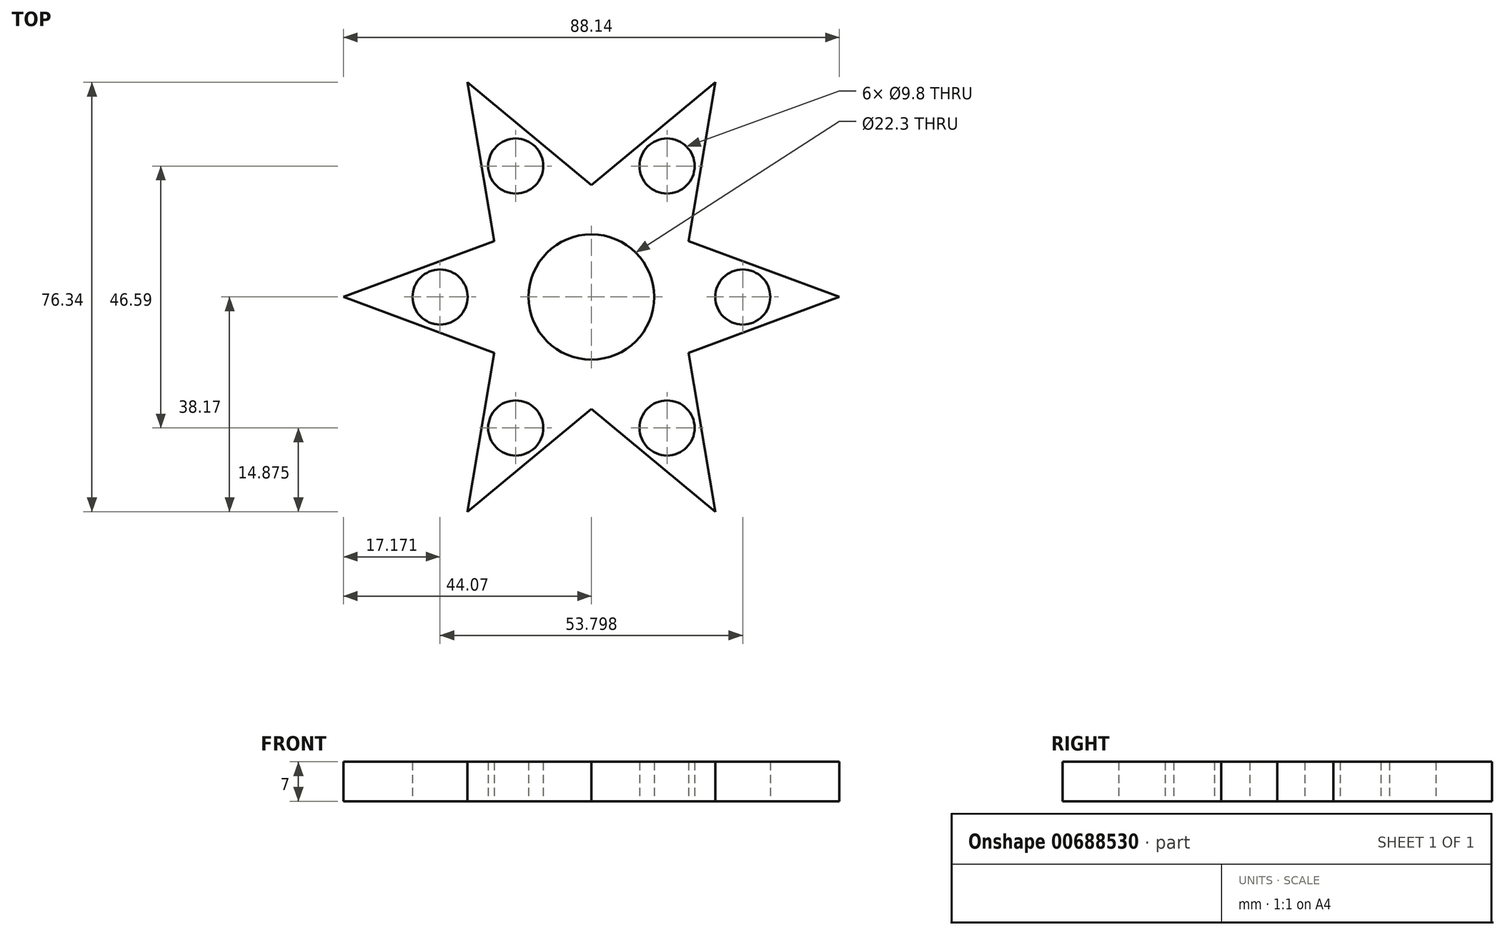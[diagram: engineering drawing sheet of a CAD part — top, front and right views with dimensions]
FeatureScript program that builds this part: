
annotation { "Feature Type Name" : "Feature", "Feature Type Description" : "" }
export const myFeature = defineFeature(function(context is Context, id is Id, definition is map)
    precondition{}
    {
        {
            var Q0;
            Q0=qCreatedBy(makeId("Top.planeOp"),FACE);
            var sketch = newSketch(context, id + "F0", { "sketchPlane" : qUnion([Q0])});
            skCircle(sketch, "E0", {"center": v(0, 0) * mm, "radius": 11.15 * mm});
            skCircle(sketch, "E1", {"center": v(0, 0) * mm, "radius": 15.38 * mm});
            skLineSegment(sketch, "E2", {"start": v(6.42, 13.98) * mm, "end": v(44.07, 0) * mm});
            skLineSegment(sketch, "E3.MirrorCS", {"start": v(6.42, -13.98) * mm, "end": v(44.07, 0) * mm});
            skCircle(sketch, "E4", {"center": v(26.9, 0) * mm, "radius": 4.9 * mm});
            skCircle(sketch, "E5.1.0", {"center": v(13.45, 23.3) * mm, "radius": 4.9 * mm});
            skLineSegment(sketch, "E5.1.1", {"start": v(-8.9, 12.55) * mm, "end": v(22.03, 38.17) * mm});
            skLineSegment(sketch, "E5.1.2", {"start": v(15.31, -1.43) * mm, "end": v(22.03, 38.17) * mm});
            skCircle(sketch, "E5.2.0", {"center": v(-13.45, 23.3) * mm, "radius": 4.9 * mm});
            skLineSegment(sketch, "E5.2.1", {"start": v(-15.31, -1.43) * mm, "end": v(-22.03, 38.17) * mm});
            skLineSegment(sketch, "E5.2.2", {"start": v(8.9, 12.55) * mm, "end": v(-22.03, 38.17) * mm});
            skCircle(sketch, "E5.3.0", {"center": v(-26.9, 0) * mm, "radius": 4.9 * mm});
            skLineSegment(sketch, "E5.3.1", {"start": v(-6.42, -13.98) * mm, "end": v(-44.07, 0) * mm});
            skLineSegment(sketch, "E5.3.2", {"start": v(-6.42, 13.98) * mm, "end": v(-44.07, 0) * mm});
            skCircle(sketch, "E5.4.0", {"center": v(-13.45, -23.3) * mm, "radius": 4.9 * mm});
            skLineSegment(sketch, "E5.4.1", {"start": v(8.9, -12.55) * mm, "end": v(-22.03, -38.17) * mm});
            skLineSegment(sketch, "E5.4.2", {"start": v(-15.31, 1.43) * mm, "end": v(-22.03, -38.17) * mm});
            skCircle(sketch, "E5.5.0", {"center": v(13.45, -23.3) * mm, "radius": 4.9 * mm});
            skLineSegment(sketch, "E5.5.1", {"start": v(15.31, 1.43) * mm, "end": v(22.03, -38.17) * mm});
            skLineSegment(sketch, "E5.5.2", {"start": v(-8.9, -12.55) * mm, "end": v(22.03, -38.17) * mm});
            skSolve(sketch);
        }
        {
            var Q0;
            Q0=makeQuery(id+"F0.imprint","IMPRINT",FACE,{"disambiguationData":[TD([[makeQuery(id+"F0.imprint","IMPRINT",EDGE,{"derivedFrom":sQuery(id+"F0.wireOp",EDGE,"E5.2.0")}),-1.0]])]});
            var Q1;
            {var subQ3=sQuery(id+"F0.wireOp",EDGE,"E2");var subQ7=sQuery(id+"F0.wireOp",EDGE,"E1");var subQ8=makeQuery(id+"F0.imprint","INTERSECT",VERTEX,{"derivedFrom":[subQ7,subQ3]});Q1=makeQuery(id+"F0.imprint","IMPRINT",FACE,{"disambiguationData":[TD([[makeQuery(id+"F0.imprint","IMPRINT",EDGE,{"disambiguationData":[TD([[subQ8,-1.0]])],"derivedFrom":subQ7}),-1.0]])]});}
            var Q2;
            Q2=makeQuery(id+"F0.imprint","IMPRINT",FACE,{"disambiguationData":[TD([[makeQuery(id+"F0.imprint","IMPRINT",EDGE,{"derivedFrom":sQuery(id+"F0.wireOp",EDGE,"E5.1.0")}),-1.0]])]});
            var Q3;
            {var subQ5=sQuery(id+"F0.wireOp",EDGE,"E5.2.2");var subQ7=sQuery(id+"F0.wireOp",EDGE,"E1");var subQ8=makeQuery(id+"F0.imprint","INTERSECT",VERTEX,{"derivedFrom":[subQ7,subQ5]});Q3=makeQuery(id+"F0.imprint","IMPRINT",FACE,{"disambiguationData":[TD([[makeQuery(id+"F0.imprint","IMPRINT",EDGE,{"disambiguationData":[TD([[subQ8,1.0]])],"derivedFrom":subQ7}),-1.0]])]});}
            var Q4;
            Q4=makeQuery(id+"F0.imprint","IMPRINT",FACE,{"disambiguationData":[TD([[makeQuery(id+"F0.imprint","IMPRINT",EDGE,{"derivedFrom":sQuery(id+"F0.wireOp",EDGE,"E4")}),-1.0]])]});
            var Q5;
            Q5=makeQuery(id+"F0.imprint","IMPRINT",FACE,{"disambiguationData":[TD([[makeQuery(id+"F0.imprint","IMPRINT",EDGE,{"derivedFrom":sQuery(id+"F0.wireOp",EDGE,"E0")}),-1.0]])]});
            var Q6;
            {var subQ0=sQuery(id+"F0.wireOp",EDGE,"E5.1.2");var subQ1=sQuery(id+"F0.wireOp",EDGE,"E1");var subQ2=makeQuery(id+"F0.imprint","INTERSECT",VERTEX,{"derivedFrom":[subQ1,subQ0]});Q6=makeQuery(id+"F0.imprint","IMPRINT",FACE,{"disambiguationData":[TD([[makeQuery(id+"F0.imprint","IMPRINT",EDGE,{"disambiguationData":[TD([[subQ2,1.0]])],"derivedFrom":subQ1}),-1.0]])]});}
            var Q7;
            Q7=makeQuery(id+"F0.imprint","IMPRINT",FACE,{"disambiguationData":[TD([[makeQuery(id+"F0.imprint","IMPRINT",EDGE,{"derivedFrom":sQuery(id+"F0.wireOp",EDGE,"E5.5.0")}),-1.0]])]});
            var Q8;
            {var subQ3=sQuery(id+"F0.wireOp",EDGE,"E3.MirrorCS");var subQ6=sQuery(id+"F0.wireOp",EDGE,"E1");var subQ9=makeQuery(id+"F0.imprint","INTERSECT",VERTEX,{"derivedFrom":[subQ6,subQ3]});Q8=makeQuery(id+"F0.imprint","IMPRINT",FACE,{"disambiguationData":[TD([[makeQuery(id+"F0.imprint","IMPRINT",EDGE,{"disambiguationData":[TD([[subQ9,1.0]])],"derivedFrom":subQ6}),-1.0]])]});}
            var Q9;
            Q9=makeQuery(id+"F0.imprint","IMPRINT",FACE,{"disambiguationData":[TD([[makeQuery(id+"F0.imprint","IMPRINT",EDGE,{"derivedFrom":sQuery(id+"F0.wireOp",EDGE,"E5.4.0")}),-1.0]])]});
            var Q10;
            {var subQ3=sQuery(id+"F0.wireOp",EDGE,"E5.2.1");var subQ7=sQuery(id+"F0.wireOp",EDGE,"E1");var subQ8=makeQuery(id+"F0.imprint","INTERSECT",VERTEX,{"derivedFrom":[subQ7,subQ3]});Q10=makeQuery(id+"F0.imprint","IMPRINT",FACE,{"disambiguationData":[TD([[makeQuery(id+"F0.imprint","IMPRINT",EDGE,{"disambiguationData":[TD([[subQ8,-1.0]])],"derivedFrom":subQ7}),-1.0]])]});}
            var Q11;
            Q11=makeQuery(id+"F0.imprint","IMPRINT",FACE,{"disambiguationData":[TD([[makeQuery(id+"F0.imprint","IMPRINT",EDGE,{"derivedFrom":sQuery(id+"F0.wireOp",EDGE,"E5.3.0")}),-1.0]])]});
            var Q12;
            {var subQ3=sQuery(id+"F0.wireOp",EDGE,"E5.1.1");var subQ7=sQuery(id+"F0.wireOp",EDGE,"E1");var subQ8=makeQuery(id+"F0.imprint","INTERSECT",VERTEX,{"derivedFrom":[subQ7,subQ3]});Q12=makeQuery(id+"F0.imprint","IMPRINT",FACE,{"disambiguationData":[TD([[makeQuery(id+"F0.imprint","IMPRINT",EDGE,{"disambiguationData":[TD([[subQ8,-1.0]])],"derivedFrom":subQ7}),-1.0]])]});}
            var Q13;
            {var subQ0=sQuery(id+"F0.wireOp",EDGE,"E2");var subQ1=sQuery(id+"F0.wireOp",EDGE,"E1");var subQ2=makeQuery(id+"F0.imprint","INTERSECT",VERTEX,{"derivedFrom":[subQ1,subQ0]});Q13=makeQuery(id+"F0.imprint","IMPRINT",FACE,{"disambiguationData":[TD([[makeQuery(id+"F0.imprint","IMPRINT",EDGE,{"disambiguationData":[TD([[subQ2,1.0]])],"derivedFrom":subQ1}),-1.0]])]});}
            var Q14;
            {var subQ0=sQuery(id+"F0.wireOp",EDGE,"E5.1.1");var subQ1=sQuery(id+"F0.wireOp",EDGE,"E1");var subQ2=makeQuery(id+"F0.imprint","INTERSECT",VERTEX,{"derivedFrom":[subQ1,subQ0]});Q14=makeQuery(id+"F0.imprint","IMPRINT",FACE,{"disambiguationData":[TD([[makeQuery(id+"F0.imprint","IMPRINT",EDGE,{"disambiguationData":[TD([[subQ2,1.0]])],"derivedFrom":subQ1}),-1.0]])]});}
            var Q15;
            {var subQ0=sQuery(id+"F0.wireOp",EDGE,"E5.2.1");var subQ1=sQuery(id+"F0.wireOp",EDGE,"E1");var subQ2=makeQuery(id+"F0.imprint","INTERSECT",VERTEX,{"derivedFrom":[subQ1,subQ0]});Q15=makeQuery(id+"F0.imprint","IMPRINT",FACE,{"disambiguationData":[TD([[makeQuery(id+"F0.imprint","IMPRINT",EDGE,{"disambiguationData":[TD([[subQ2,1.0]])],"derivedFrom":subQ1}),-1.0]])]});}
            var Q16;
            {var subQ0=sQuery(id+"F0.wireOp",EDGE,"E5.3.1");var subQ1=sQuery(id+"F0.wireOp",EDGE,"E1");var subQ2=makeQuery(id+"F0.imprint","INTERSECT",VERTEX,{"derivedFrom":[subQ1,subQ0]});Q16=makeQuery(id+"F0.imprint","IMPRINT",FACE,{"disambiguationData":[TD([[makeQuery(id+"F0.imprint","IMPRINT",EDGE,{"disambiguationData":[TD([[subQ2,1.0]])],"derivedFrom":subQ1}),-1.0]])]});}
            var Q17;
            {var subQ0=sQuery(id+"F0.wireOp",EDGE,"E3.MirrorCS");var subQ1=sQuery(id+"F0.wireOp",EDGE,"E1");var subQ2=makeQuery(id+"F0.imprint","INTERSECT",VERTEX,{"derivedFrom":[subQ1,subQ0]});Q17=makeQuery(id+"F0.imprint","IMPRINT",FACE,{"disambiguationData":[TD([[makeQuery(id+"F0.imprint","IMPRINT",EDGE,{"disambiguationData":[TD([[subQ2,-1.0]])],"derivedFrom":subQ1}),-1.0]])]});}
            var Q18;
            {var subQ0=sQuery(id+"F0.wireOp",EDGE,"E5.1.2");var subQ1=sQuery(id+"F0.wireOp",EDGE,"E1");var subQ2=makeQuery(id+"F0.imprint","INTERSECT",VERTEX,{"derivedFrom":[subQ1,subQ0]});Q18=makeQuery(id+"F0.imprint","IMPRINT",FACE,{"disambiguationData":[TD([[makeQuery(id+"F0.imprint","IMPRINT",EDGE,{"disambiguationData":[TD([[subQ2,-1.0]])],"derivedFrom":subQ1}),-1.0]])]});}
            extrude(context, id + "F1", {"entities" : qUnion([Q0, Q1, Q2, Q3, Q4, Q5, Q6, Q7, Q8, Q9, Q10, Q11, Q12, Q13, Q14, Q15, Q16, Q17, Q18]), "depth" : 7 * mm, "offsetDistance" : 25 * mm});
        }
    });
